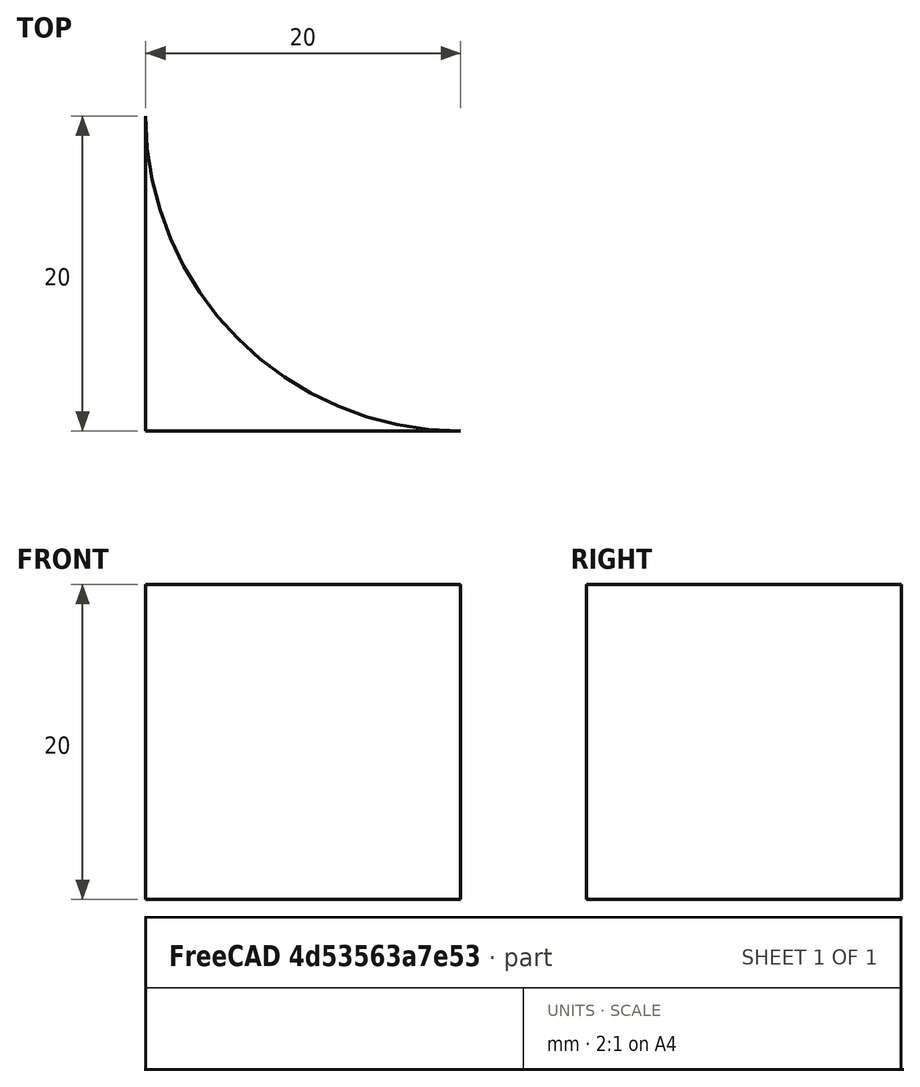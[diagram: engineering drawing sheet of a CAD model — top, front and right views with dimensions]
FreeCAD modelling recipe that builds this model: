
FCSTD DOCUMENT  (FreeCAD 0.20R27319 (Git))
Label: Router Corners
License: All rights reserved
LicenseURL: http://en.wikipedia.org/wiki/All_rights_reserved
objects: Sketcher::SketchObject×1, PartDesign::Pad×1, PartDesign::Body×1
note: 4 computed .brp shape members not serialized (recipe doc carries the construction recipe); baked Part::Feature solids carry a one-line shape summary decoded from their .brp

FEATURE [Sketcher::SketchObject] Sketch
  FullyConstrained = true
  MapMode = 5
  Support = -> [XY_Plane]
  sketch-geometry (3):
    g0: LineSegment StartX=0 StartY=0 StartZ=0 EndX=20 EndY=0 EndZ=0
    g1: LineSegment StartX=0 StartY=0 StartZ=0 EndX=0 EndY=20 EndZ=0
    g2: ArcOfCircle CenterX=20 CenterY=20 CenterZ=0 NormalX=0 NormalY=0 NormalZ=1 AngleXU=0 Radius=20 StartAngle=3.14159 EndAngle=4.71239
  constraints (9):
    c: Coincident(g0,g-1)
    c: PointOnObject(g0,g-1)
    c: Coincident(g1,g0)
    c: PointOnObject(g1,g-2)
    c: DistanceY(g1,g1) = 20
    c: DistanceX(g0,g0) = 20
    c: Coincident(g2,g1)
    c: Coincident(g2,g0)
    c: DistanceX(g2) = 20
FEATURE [PartDesign::Pad] Pad
  Direction = (0,0,1)
  Length = 20
  Length2 = 10
  Profile = -> Sketch
  ReferenceAxis = -> Sketch [N_Axis]
  Type = 0
FEATURE [PartDesign::Body] Body
  Group = -> [Sketch,Pad]
  Origin = -> Origin
  Tip = -> Pad
